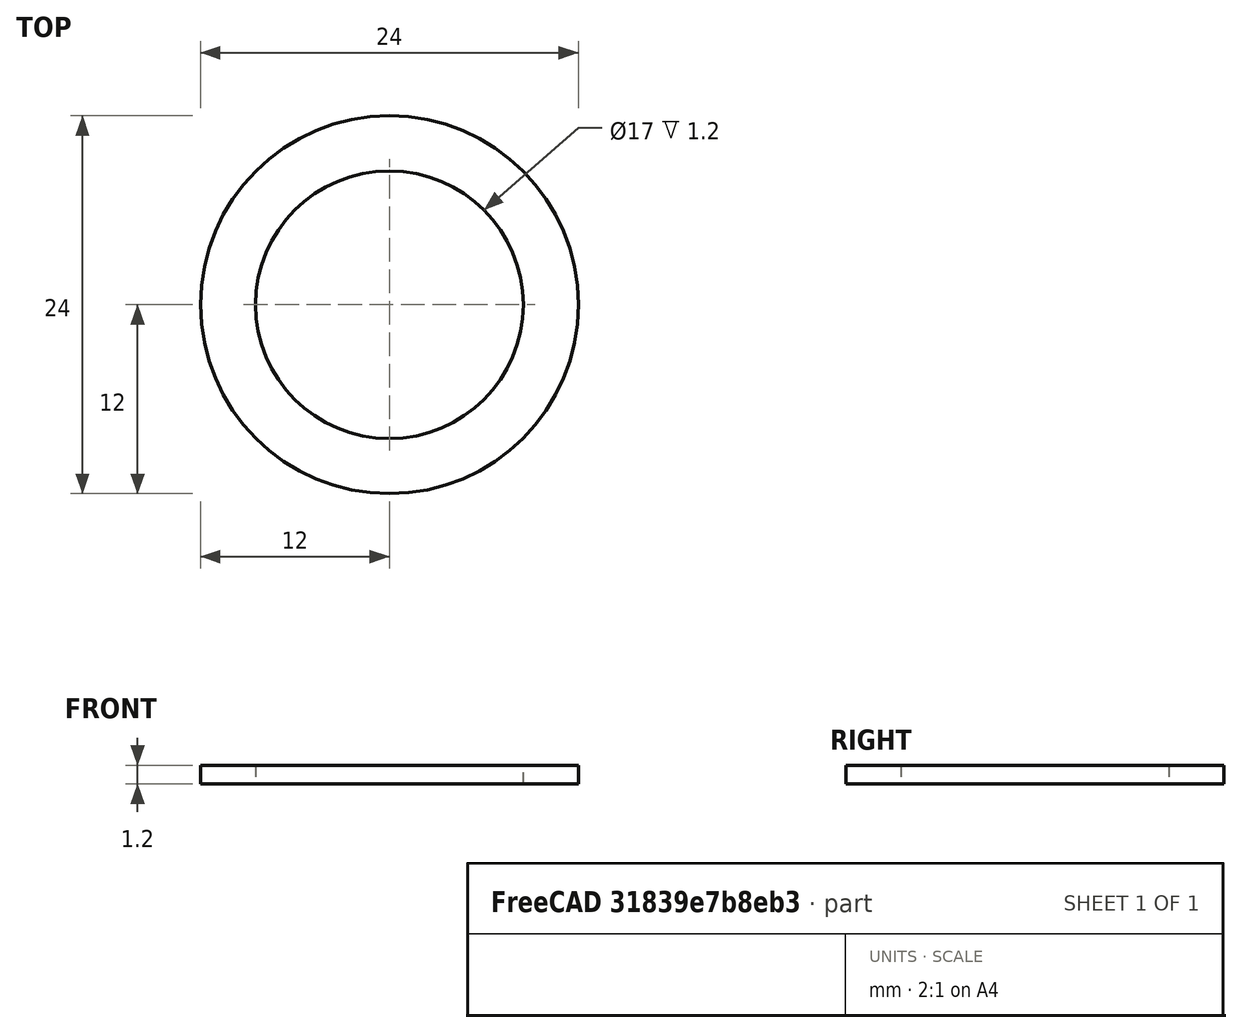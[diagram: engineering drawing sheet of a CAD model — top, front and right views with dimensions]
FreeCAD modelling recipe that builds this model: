
FCSTD DOCUMENT  (FreeCAD 0.19R24276 (Git))
Label: Ring_d17_d24_h1_2
License: All rights reserved
LicenseURL: http://en.wikipedia.org/wiki/All_rights_reserved
objects: Sketcher::SketchObject×1, PartDesign::Pad×1, PartDesign::Body×1
note: 4 computed .brp shape members not serialized (recipe doc carries the construction recipe); baked Part::Feature solids carry a one-line shape summary decoded from their .brp

FEATURE [Sketcher::SketchObject] Sketch
  FullyConstrained = true
  MapMode = 5
  Support = -> [XY_Plane]
  sketch-geometry (2):
    g0: Circle CenterX=0 CenterY=0 CenterZ=0 NormalX=0 NormalY=0 NormalZ=1 AngleXU=0 Radius=12
    g1: Circle CenterX=0 CenterY=0 CenterZ=0 NormalX=0 NormalY=0 NormalZ=1 AngleXU=0 Radius=8.5
  constraints (4):
    c: Coincident(g0,g-1)
    c: Coincident(g1,g-1)
    c: Diameter(g0) = 24
    c: Diameter(g1) = 17
FEATURE [PartDesign::Pad] Pad
  Direction = (1,1,1)
  Length = 1.2
  Length2 = 100
  Profile = -> Sketch
  Type = 0
FEATURE [PartDesign::Body] Body
  Group = -> [Sketch,Pad]
  Origin = -> Origin
  Tip = -> Pad
